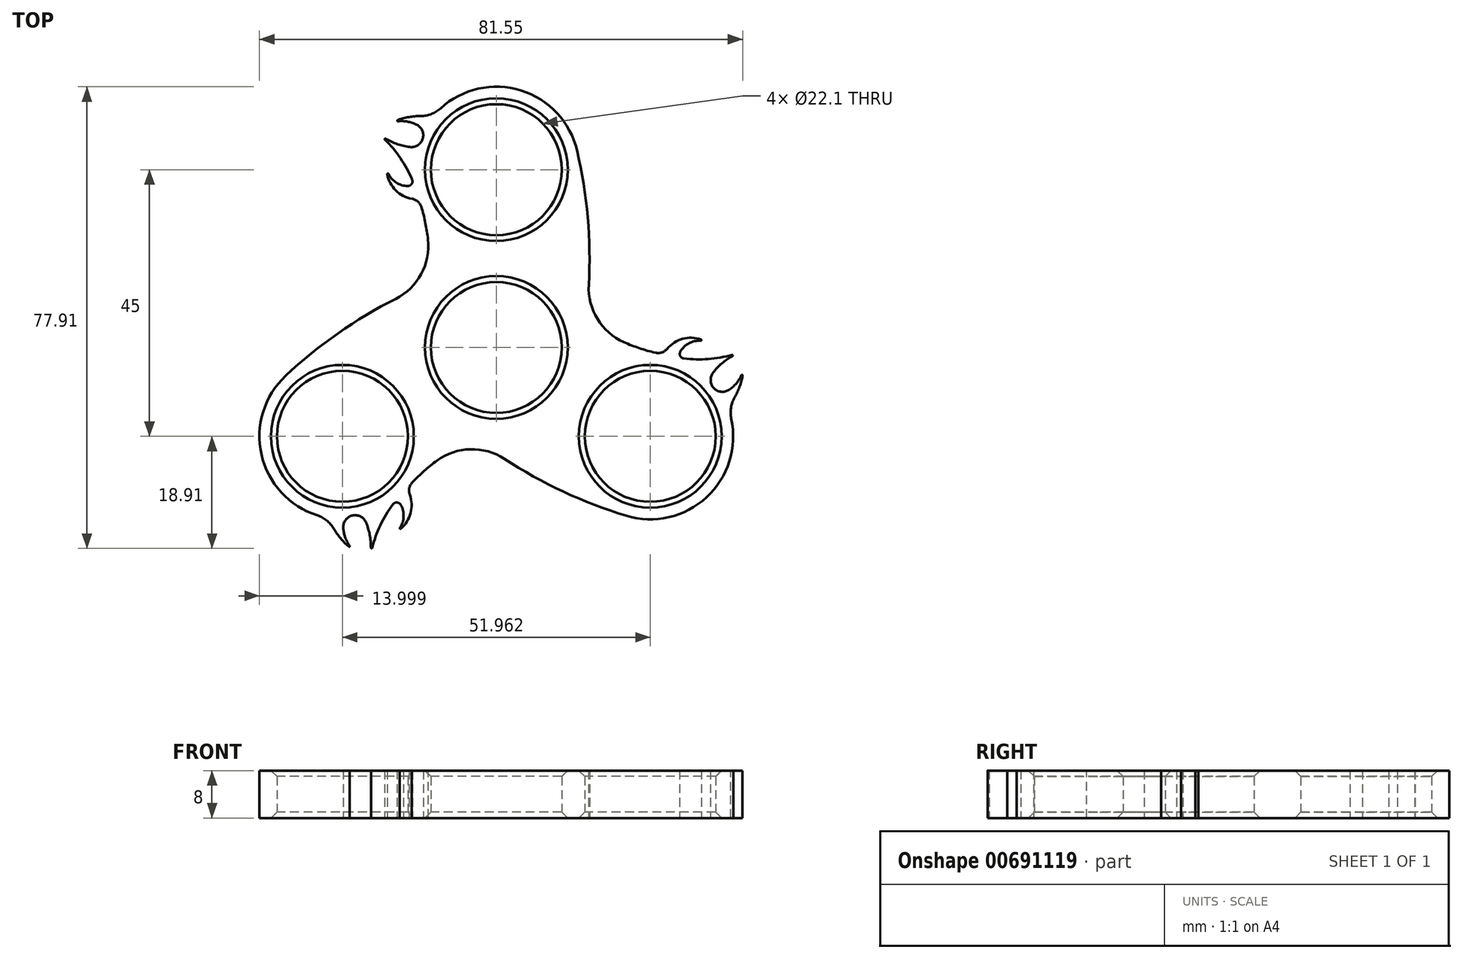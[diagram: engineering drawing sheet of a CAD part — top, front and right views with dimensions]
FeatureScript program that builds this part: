
annotation { "Feature Type Name" : "Feature", "Feature Type Description" : "" }
export const myFeature = defineFeature(function(context is Context, id is Id, definition is map)
    precondition{}
    {
        {
            var Q0;
            Q0=qCreatedBy(makeId("Top.planeOp"),FACE);
            var sketch = newSketch(context, id + "F0", { "sketchPlane" : qUnion([Q0])});
            skArc(sketch, "E0", {"start": v(-13.16, 4.77) * mm, "mid": v(-3.98, -13.42) * mm, "end": v(13.63, -3.18) * mm});
            skArc(sketch, "E1", {"start": v(13.63, 33.18) * mm, "mid": v(3.19, 43.63) * mm, "end": v(-10.81, 38.9) * mm});
            skLineSegment(sketch, "E2", {"start": v(-41.88, 30) * mm, "end": v(59.47, 30) * mm, "construction": true});
            skArc(sketch, "E3.trimOffspring", {"start": v(-13.16, 4.77) * mm, "mid": v(-11.38, 14.2) * mm, "end": v(-12.65, 23.7) * mm});
            skArc(sketch, "E4.trimOffspring", {"start": v(13.63, -3.18) * mm, "mid": v(15.73, 15) * mm, "end": v(13.63, 33.18) * mm});
            skCircle(sketch, "E5", {"center": v(0, 0) * mm, "radius": 11.05 * mm});
            skCircle(sketch, "E6", {"center": v(0, 30) * mm, "radius": 11.05 * mm});
            skCircle(sketch, "E7", {"center": v(39.97, 55.34) * mm, "radius": 10 * mm});
            skPoint(sketch, "E8.visualSharp", {"position": v(-13.67, 33.03) * mm});
            skArc(sketch, "E9.trimOffspring", {"start": v(-13.44, 37.6) * mm, "mid": v(-15, 38.1) * mm, "end": v(-16.62, 38.18) * mm});
            skArc(sketch, "E10.trimOffspring", {"start": v(-10.81, 38.9) * mm, "mid": v(-13.77, 39) * mm, "end": v(-16.66, 38.37) * mm});
            skArc(sketch, "E11", {"start": v(-18.7, 35.23) * mm, "mid": v(-16.71, 34.32) * mm, "end": v(-14.6, 33.82) * mm});
            skArc(sketch, "E12.filletArc", {"start": v(-14.6, 33.82) * mm, "mid": v(-12.42, 35.22) * mm, "end": v(-13.44, 37.6) * mm});
            skArc(sketch, "E13", {"start": v(-18.42, 29.25) * mm, "mid": v(-16.97, 26.5) * mm, "end": v(-14.22, 25.08) * mm});
            skArc(sketch, "E14.filletArc", {"start": v(-12.65, 23.7) * mm, "mid": v(-13.24, 24.61) * mm, "end": v(-14.22, 25.08) * mm});
            skArc(sketch, "E15", {"start": v(-18.24, 29.31) * mm, "mid": v(-16.88, 27.82) * mm, "end": v(-14.96, 27.24) * mm});
            skArc(sketch, "E16.trimOffspring", {"start": v(-14.21, 28.35) * mm, "mid": v(-16.18, 31.94) * mm, "end": v(-18.81, 35.08) * mm});
            skPoint(sketch, "E17.visualSharp", {"position": v(-13.84, 27.4) * mm});
            skArc(sketch, "E17.filletArc", {"start": v(-14.96, 27.24) * mm, "mid": v(-14.29, 27.6) * mm, "end": v(-14.21, 28.35) * mm});
            skPoint(sketch, "E18.visualSharp", {"position": v(-20.41, 36.5) * mm});
            skArc(sketch, "E18.filletArc", {"start": v(-18.7, 35.23) * mm, "mid": v(-18.82, 35.2) * mm, "end": v(-18.81, 35.08) * mm});
            skPoint(sketch, "E19.visualSharp", {"position": v(-17.55, 38.02) * mm});
            skArc(sketch, "E19.filletArc", {"start": v(-16.66, 38.37) * mm, "mid": v(-16.73, 38.26) * mm, "end": v(-16.62, 38.18) * mm});
            skPoint(sketch, "E20.visualSharp", {"position": v(-18.5, 30.04) * mm});
            skArc(sketch, "E20.filletArc", {"start": v(-18.24, 29.31) * mm, "mid": v(-18.36, 29.36) * mm, "end": v(-18.42, 29.25) * mm});
            skSolve(sketch);
        }
        {
            var Q0;
            Q0=makeQuery(id+"F0.imprint","IMPRINT",FACE,{"disambiguationData":[TD([[makeQuery(id+"F0.imprint","IMPRINT",EDGE,{"derivedFrom":sQuery(id+"F0.wireOp",EDGE,"E0")}),1.0]])]});
            extrude(context, id + "F1", {"entities" : qUnion([Q0]), "depth" : 8 * mm, "offsetDistance" : 25 * mm});
        }
        {
            var Q0;
            Q0=makeQuery(id+"F1.opExtrude","SWEPT_BODY",BODY,{"disambiguationData":[OSD([sQuery(id+"F0.wireOp",EDGE,"E0"),sQuery(id+"F0.wireOp",EDGE,"E1"),sQuery(id+"F0.wireOp",EDGE,"E3.trimOffspring"),sQuery(id+"F0.wireOp",EDGE,"E4.trimOffspring"),sQuery(id+"F0.wireOp",EDGE,"E5"),sQuery(id+"F0.wireOp",EDGE,"E6")])]});
            var Q1;
            Q1=makeQuery(id+"F1.opExtrude","SWEPT_FACE",FACE,{"disambiguationData":[OSD([sQuery(id+"F0.wireOp",EDGE,"E5")])]});
            circularPattern(context, id + "F2", {"operationType" : NewBodyOperationType.ADD, "entities" : qUnion([Q0]), "axis" : qUnion([Q1]), "angle" : 360 * degree, "instanceCount" : 3, "equalSpace" : true});
        }
        {
            var Q0;
            Q0=makeQuery(id+"F2.boolean.opBoolean","INTERSECT",EDGE,{"derivedFrom":[makeQuery(id+"F1.opExtrude","SWEPT_FACE",FACE,{"disambiguationData":[OSD([sQuery(id+"F0.wireOp",EDGE,"E4.trimOffspring")])]}),makeQuery(id+"F2.opPattern","COPY",FACE,{"derivedFrom":makeQuery(id+"F1.opExtrude","SWEPT_FACE",FACE,{"disambiguationData":[OSD([sQuery(id+"F0.wireOp",EDGE,"E3.trimOffspring")])]}),"instanceName":"2"})]});
            var Q1;
            Q1=makeQuery(id+"F2.boolean.opBoolean","INTERSECT",EDGE,{"derivedFrom":[makeQuery(id+"F2.opPattern","COPY",FACE,{"derivedFrom":makeQuery(id+"F1.opExtrude","SWEPT_FACE",FACE,{"disambiguationData":[OSD([sQuery(id+"F0.wireOp",EDGE,"E3.trimOffspring")])]}),"instanceName":"1"}),makeQuery(id+"F2.opPattern","COPY",FACE,{"derivedFrom":makeQuery(id+"F1.opExtrude","SWEPT_FACE",FACE,{"disambiguationData":[OSD([sQuery(id+"F0.wireOp",EDGE,"E4.trimOffspring")])]}),"instanceName":"2"})]});
            var Q2;
            Q2=makeQuery(id+"F2.boolean.opBoolean","INTERSECT",EDGE,{"derivedFrom":[makeQuery(id+"F1.opExtrude","SWEPT_FACE",FACE,{"disambiguationData":[OSD([sQuery(id+"F0.wireOp",EDGE,"E3.trimOffspring")])]}),makeQuery(id+"F2.opPattern","COPY",FACE,{"derivedFrom":makeQuery(id+"F1.opExtrude","SWEPT_FACE",FACE,{"disambiguationData":[OSD([sQuery(id+"F0.wireOp",EDGE,"E4.trimOffspring")])]}),"instanceName":"1"})]});
            fillet(context, id + "F3", {"entities" : qUnion([Q0, Q1, Q2]), "radius" : 10 * mm, "tangentPropagation" : true, "allowEdgeOverflow" : false});
        }
        {
            var Q0;
            Q0=makeQuery(id+"F2.opPattern","COPY",EDGE,{"derivedFrom":makeQuery(id+"F1.opExtrude","SWEPT_EDGE",EDGE,{"disambiguationData":[OSD([sQuery(id+"F0.wireOp",EDGE,"E1"),sQuery(id+"F0.wireOp",EDGE,"E10.trimOffspring")])]}),"instanceName":"2"});
            var Q1;
            Q1=makeQuery(id+"F2.opPattern","COPY",EDGE,{"derivedFrom":makeQuery(id+"F1.opExtrude","SWEPT_EDGE",EDGE,{"disambiguationData":[OSD([sQuery(id+"F0.wireOp",EDGE,"E1"),sQuery(id+"F0.wireOp",EDGE,"E10.trimOffspring")])]}),"instanceName":"1"});
            var Q2;
            Q2=makeQuery(id+"F1.opExtrude","SWEPT_EDGE",EDGE,{"disambiguationData":[OSD([sQuery(id+"F0.wireOp",EDGE,"E1"),sQuery(id+"F0.wireOp",EDGE,"E10.trimOffspring")])]});
            fillet(context, id + "F4", {"entities" : qUnion([Q0, Q1, Q2]), "radius" : 5 * mm, "tangentPropagation" : true, "allowEdgeOverflow" : false});
        }
        {
            var Q0;
            Q0=makeQuery(id+"F1.opExtrude","CAP_EDGE",EDGE,{"disambiguationData":[OSD([sQuery(id+"F0.wireOp",EDGE,"E6")])],"isStart":false});
            var Q1;
            Q1=makeQuery(id+"F1.opExtrude","CAP_EDGE",EDGE,{"disambiguationData":[OSD([sQuery(id+"F0.wireOp",EDGE,"E6")])],"isStart":true});
            var Q2;
            Q2=makeQuery(id+"F1.opExtrude","CAP_EDGE",EDGE,{"disambiguationData":[OSD([sQuery(id+"F0.wireOp",EDGE,"E5")])],"isStart":false});
            var Q3;
            Q3=makeQuery(id+"F1.opExtrude","CAP_EDGE",EDGE,{"disambiguationData":[OSD([sQuery(id+"F0.wireOp",EDGE,"E5")])],"isStart":true});
            var Q4;
            Q4=makeQuery(id+"F2.opPattern","COPY",EDGE,{"derivedFrom":makeQuery(id+"F1.opExtrude","CAP_EDGE",EDGE,{"disambiguationData":[OSD([sQuery(id+"F0.wireOp",EDGE,"E6")])],"isStart":false}),"instanceName":"1"});
            var Q5;
            Q5=makeQuery(id+"F2.opPattern","COPY",EDGE,{"derivedFrom":makeQuery(id+"F1.opExtrude","CAP_EDGE",EDGE,{"disambiguationData":[OSD([sQuery(id+"F0.wireOp",EDGE,"E6")])],"isStart":true}),"instanceName":"1"});
            var Q6;
            Q6=makeQuery(id+"F2.opPattern","COPY",EDGE,{"derivedFrom":makeQuery(id+"F1.opExtrude","CAP_EDGE",EDGE,{"disambiguationData":[OSD([sQuery(id+"F0.wireOp",EDGE,"E6")])],"isStart":false}),"instanceName":"2"});
            var Q7;
            Q7=makeQuery(id+"F2.opPattern","COPY",EDGE,{"derivedFrom":makeQuery(id+"F1.opExtrude","CAP_EDGE",EDGE,{"disambiguationData":[OSD([sQuery(id+"F0.wireOp",EDGE,"E6")])],"isStart":true}),"instanceName":"2"});
            chamfer(context, id + "F5", {"entities" : qUnion([Q0, Q1, Q2, Q3, Q4, Q5, Q6, Q7]), "width" : 1 * mm, "tangentPropagation" : true});
        }
    });
